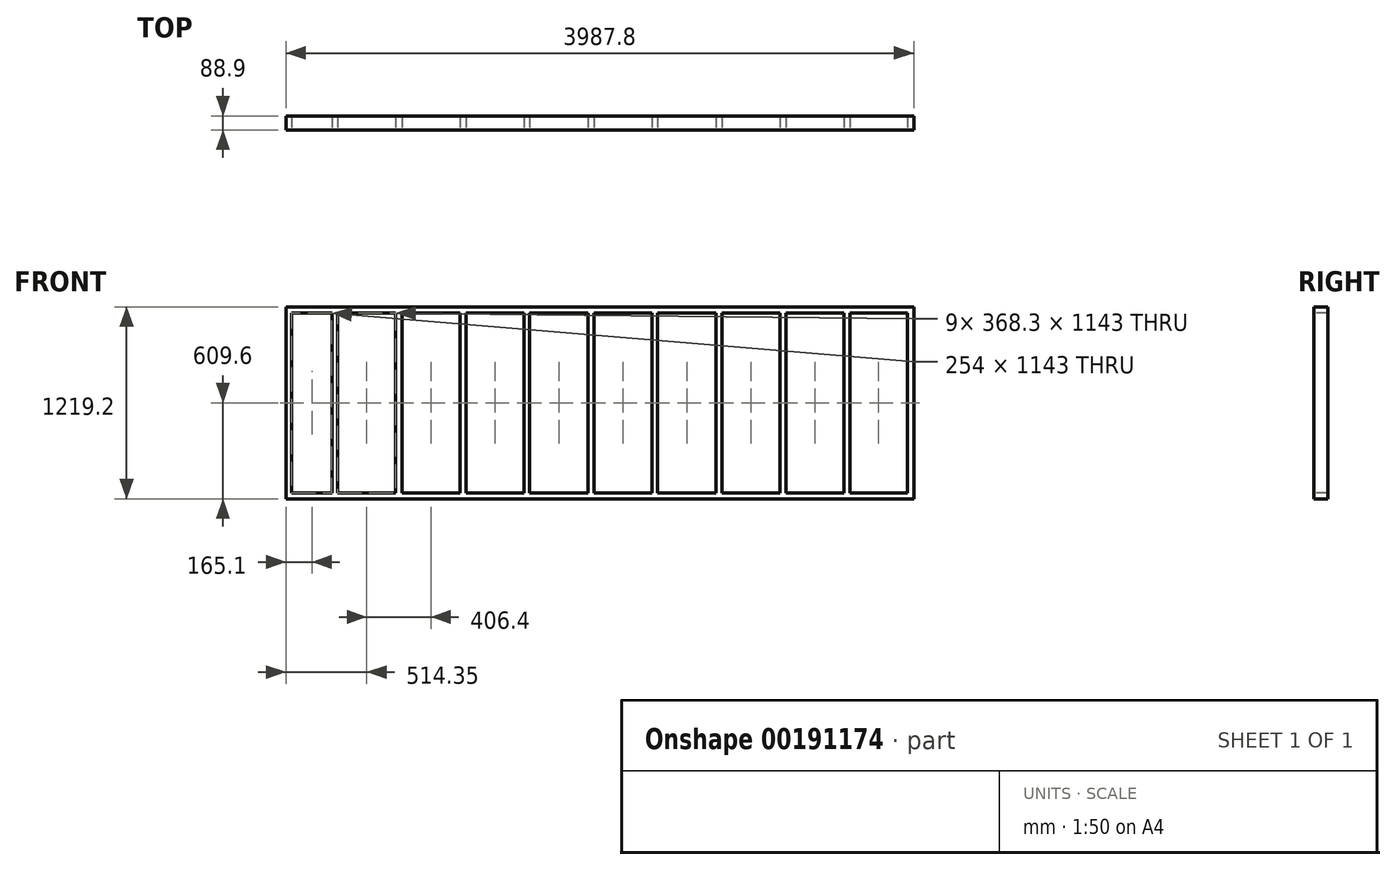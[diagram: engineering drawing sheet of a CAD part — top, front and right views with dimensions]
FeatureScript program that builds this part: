
annotation { "Feature Type Name" : "Feature", "Feature Type Description" : "" }
export const myFeature = defineFeature(function(context is Context, id is Id, definition is map)
    precondition{}
    {
        {
            var Q0;
            Q0=qCreatedBy(makeId("Top.planeOp"),FACE);
            var sketch = newSketch(context, id + "F0", { "sketchPlane" : qUnion([Q0])});
            skLineSegment(sketch, "E0.bottom", {"start": v(1993.9, -44.45) * mm, "end": v(-1993.9, -44.45) * mm});
            skLineSegment(sketch, "E0.top", {"start": v(1993.9, 44.45) * mm, "end": v(-1993.9, 44.45) * mm});
            skLineSegment(sketch, "E0.left", {"start": v(1993.9, -44.45) * mm, "end": v(1993.9, 44.45) * mm});
            skLineSegment(sketch, "E0.right", {"start": v(-1993.9, -44.45) * mm, "end": v(-1993.9, 44.45) * mm});
            skPoint(sketch, "E0.middle", {"position": v(0, 0) * mm});
            skSolve(sketch);
        }
        {
            var Q0;
            Q0 = qSketchRegion(id + "F0", true);
            extrude(context, id + "F1", {"entities" : qUnion([Q0]), "depth" : 38.1 * mm});
        }
        {
            var Q0;
            Q0=makeQuery(id+"F1.opExtrude","CAP_FACE",FACE,{"disambiguationData":[OSD([sQuery(id+"F0.wireOp",EDGE,"E0.bottom"),sQuery(id+"F0.wireOp",EDGE,"E0.top"),sQuery(id+"F0.wireOp",EDGE,"E0.left"),sQuery(id+"F0.wireOp",EDGE,"E0.right")])],"isStart":false});
            var sketch = newSketch(context, id + "F2", { "sketchPlane" : qUnion([Q0])});
            skLineSegment(sketch, "E1.bottom", {"start": v(1993.9, 44.45) * mm, "end": v(1955.8, 44.45) * mm});
            skLineSegment(sketch, "E1.top", {"start": v(1993.9, -44.45) * mm, "end": v(1955.8, -44.45) * mm});
            skLineSegment(sketch, "E1.left", {"start": v(1993.9, 44.45) * mm, "end": v(1993.9, -44.45) * mm});
            skLineSegment(sketch, "E1.right", {"start": v(1955.8, 44.45) * mm, "end": v(1955.8, -44.45) * mm});
            skLineSegment(sketch, "E2.bottom", {"start": v(1587.5, 44.45) * mm, "end": v(1549.4, 44.45) * mm});
            skLineSegment(sketch, "E2.top", {"start": v(1587.5, -44.45) * mm, "end": v(1549.4, -44.45) * mm});
            skLineSegment(sketch, "E2.left", {"start": v(1587.5, 44.45) * mm, "end": v(1587.5, -44.45) * mm});
            skLineSegment(sketch, "E2.right", {"start": v(1549.4, 44.45) * mm, "end": v(1549.4, -44.45) * mm});
            skLineSegment(sketch, "E3.bottom", {"start": v(1181.1, 44.45) * mm, "end": v(1143, 44.45) * mm});
            skLineSegment(sketch, "E3.top", {"start": v(1181.1, -44.45) * mm, "end": v(1143, -44.45) * mm});
            skLineSegment(sketch, "E3.left", {"start": v(1181.1, 44.45) * mm, "end": v(1181.1, -44.45) * mm});
            skLineSegment(sketch, "E3.right", {"start": v(1143, 44.45) * mm, "end": v(1143, -44.45) * mm});
            skLineSegment(sketch, "E4.bottom", {"start": v(774.7, 44.45) * mm, "end": v(736.6, 44.45) * mm});
            skLineSegment(sketch, "E4.top", {"start": v(774.7, -44.45) * mm, "end": v(736.6, -44.45) * mm});
            skLineSegment(sketch, "E4.left", {"start": v(774.7, 44.45) * mm, "end": v(774.7, -44.45) * mm});
            skLineSegment(sketch, "E4.right", {"start": v(736.6, 44.45) * mm, "end": v(736.6, -44.45) * mm});
            skLineSegment(sketch, "E5.bottom", {"start": v(368.3, 44.45) * mm, "end": v(330.2, 44.45) * mm});
            skLineSegment(sketch, "E5.top", {"start": v(368.3, -44.45) * mm, "end": v(330.2, -44.45) * mm});
            skLineSegment(sketch, "E5.left", {"start": v(368.3, 44.45) * mm, "end": v(368.3, -44.45) * mm});
            skLineSegment(sketch, "E5.right", {"start": v(330.2, 44.45) * mm, "end": v(330.2, -44.45) * mm});
            skLineSegment(sketch, "E6.bottom", {"start": v(-38.1, 44.45) * mm, "end": v(-76.2, 44.45) * mm});
            skLineSegment(sketch, "E6.top", {"start": v(-38.1, -44.45) * mm, "end": v(-76.2, -44.45) * mm});
            skLineSegment(sketch, "E6.left", {"start": v(-38.1, 44.45) * mm, "end": v(-38.1, -44.45) * mm});
            skLineSegment(sketch, "E6.right", {"start": v(-76.2, 44.45) * mm, "end": v(-76.2, -44.45) * mm});
            skLineSegment(sketch, "E7.bottom", {"start": v(-444.5, 44.45) * mm, "end": v(-482.6, 44.45) * mm});
            skLineSegment(sketch, "E7.top", {"start": v(-444.5, -44.45) * mm, "end": v(-482.6, -44.45) * mm});
            skLineSegment(sketch, "E7.left", {"start": v(-444.5, 44.45) * mm, "end": v(-444.5, -44.45) * mm});
            skLineSegment(sketch, "E7.right", {"start": v(-482.6, 44.45) * mm, "end": v(-482.6, -44.45) * mm});
            skLineSegment(sketch, "E8.bottom", {"start": v(-850.9, 44.45) * mm, "end": v(-889, 44.45) * mm});
            skLineSegment(sketch, "E8.top", {"start": v(-850.9, -44.45) * mm, "end": v(-889, -44.45) * mm});
            skLineSegment(sketch, "E8.left", {"start": v(-850.9, 44.45) * mm, "end": v(-850.9, -44.45) * mm});
            skLineSegment(sketch, "E8.right", {"start": v(-889, 44.45) * mm, "end": v(-889, -44.45) * mm});
            skLineSegment(sketch, "E9.bottom", {"start": v(-1257.3, 44.45) * mm, "end": v(-1295.4, 44.45) * mm});
            skLineSegment(sketch, "E9.top", {"start": v(-1257.3, -44.45) * mm, "end": v(-1295.4, -44.45) * mm});
            skLineSegment(sketch, "E9.left", {"start": v(-1257.3, 44.45) * mm, "end": v(-1257.3, -44.45) * mm});
            skLineSegment(sketch, "E9.right", {"start": v(-1295.4, 44.45) * mm, "end": v(-1295.4, -44.45) * mm});
            skLineSegment(sketch, "E10.bottom", {"start": v(-1993.9, 44.45) * mm, "end": v(-1955.8, 44.45) * mm});
            skLineSegment(sketch, "E10.top", {"start": v(-1993.9, -44.45) * mm, "end": v(-1955.8, -44.45) * mm});
            skLineSegment(sketch, "E10.left", {"start": v(-1993.9, 44.45) * mm, "end": v(-1993.9, -44.45) * mm});
            skLineSegment(sketch, "E10.right", {"start": v(-1955.8, 44.45) * mm, "end": v(-1955.8, -44.45) * mm});
            skLineSegment(sketch, "E11.bottom", {"start": v(-1701.8, 44.45) * mm, "end": v(-1663.7, 44.45) * mm});
            skLineSegment(sketch, "E11.top", {"start": v(-1701.8, -44.45) * mm, "end": v(-1663.7, -44.45) * mm});
            skLineSegment(sketch, "E11.left", {"start": v(-1701.8, 44.45) * mm, "end": v(-1701.8, -44.45) * mm});
            skLineSegment(sketch, "E11.right", {"start": v(-1663.7, 44.45) * mm, "end": v(-1663.7, -44.45) * mm});
            skSolve(sketch);
        }
        {
            var Q0;
            Q0 = qSketchRegion(id + "F2", true);
            extrude(context, id + "F3", {"entities" : qUnion([Q0]), "operationType" : NewBodyOperationType.ADD, "depth" : 1143 * mm});
        }
        {
            var Q0;
            Q0=makeQuery(id+"F3.boolean.opBoolean","MERGE",FACE,{"derivedFrom":[makeQuery(id+"F1.opExtrude","SWEPT_FACE",FACE,{"disambiguationData":[OSD([sQuery(id+"F0.wireOp",EDGE,"E0.bottom")])]}),makeQuery(id+"F3.opExtrude","SWEPT_FACE",FACE,{"disambiguationData":[OSD([sQuery(id+"F2.wireOp",EDGE,"E1.top")])]}),makeQuery(id+"F3.opExtrude","SWEPT_FACE",FACE,{"disambiguationData":[OSD([sQuery(id+"F2.wireOp",EDGE,"E2.top")])]}),makeQuery(id+"F3.opExtrude","SWEPT_FACE",FACE,{"disambiguationData":[OSD([sQuery(id+"F2.wireOp",EDGE,"E3.top")])]}),makeQuery(id+"F3.opExtrude","SWEPT_FACE",FACE,{"disambiguationData":[OSD([sQuery(id+"F2.wireOp",EDGE,"E4.top")])]}),makeQuery(id+"F3.opExtrude","SWEPT_FACE",FACE,{"disambiguationData":[OSD([sQuery(id+"F2.wireOp",EDGE,"E5.top")])]}),makeQuery(id+"F3.opExtrude","SWEPT_FACE",FACE,{"disambiguationData":[OSD([sQuery(id+"F2.wireOp",EDGE,"E6.top")])]}),makeQuery(id+"F3.opExtrude","SWEPT_FACE",FACE,{"disambiguationData":[OSD([sQuery(id+"F2.wireOp",EDGE,"E7.top")])]}),makeQuery(id+"F3.opExtrude","SWEPT_FACE",FACE,{"disambiguationData":[OSD([sQuery(id+"F2.wireOp",EDGE,"E8.top")])]}),makeQuery(id+"F3.opExtrude","SWEPT_FACE",FACE,{"disambiguationData":[OSD([sQuery(id+"F2.wireOp",EDGE,"E9.top")])]}),makeQuery(id+"F3.opExtrude","SWEPT_FACE",FACE,{"disambiguationData":[OSD([sQuery(id+"F2.wireOp",EDGE,"E10.top")])]}),makeQuery(id+"F3.opExtrude","SWEPT_FACE",FACE,{"disambiguationData":[OSD([sQuery(id+"F2.wireOp",EDGE,"E11.top")])]})]});
            var sketch = newSketch(context, id + "F4", { "sketchPlane" : qUnion([Q0])});
            skLineSegment(sketch, "E12.bottom", {"start": v(-1993.9, 1181.1) * mm, "end": v(1993.9, 1181.1) * mm});
            skLineSegment(sketch, "E12.top", {"start": v(-1993.9, 1219.2) * mm, "end": v(1993.9, 1219.2) * mm});
            skLineSegment(sketch, "E12.left", {"start": v(-1993.9, 1181.1) * mm, "end": v(-1993.9, 1219.2) * mm});
            skLineSegment(sketch, "E12.right", {"start": v(1993.9, 1181.1) * mm, "end": v(1993.9, 1219.2) * mm});
            skSolve(sketch);
        }
        {
            var Q0;
            Q0 = qSketchRegion(id + "F4", true);
            extrude(context, id + "F5", {"entities" : qUnion([Q0]), "operationType" : NewBodyOperationType.ADD, "oppositeDirection" : true, "depth" : 88.9 * mm});
        }
    });
